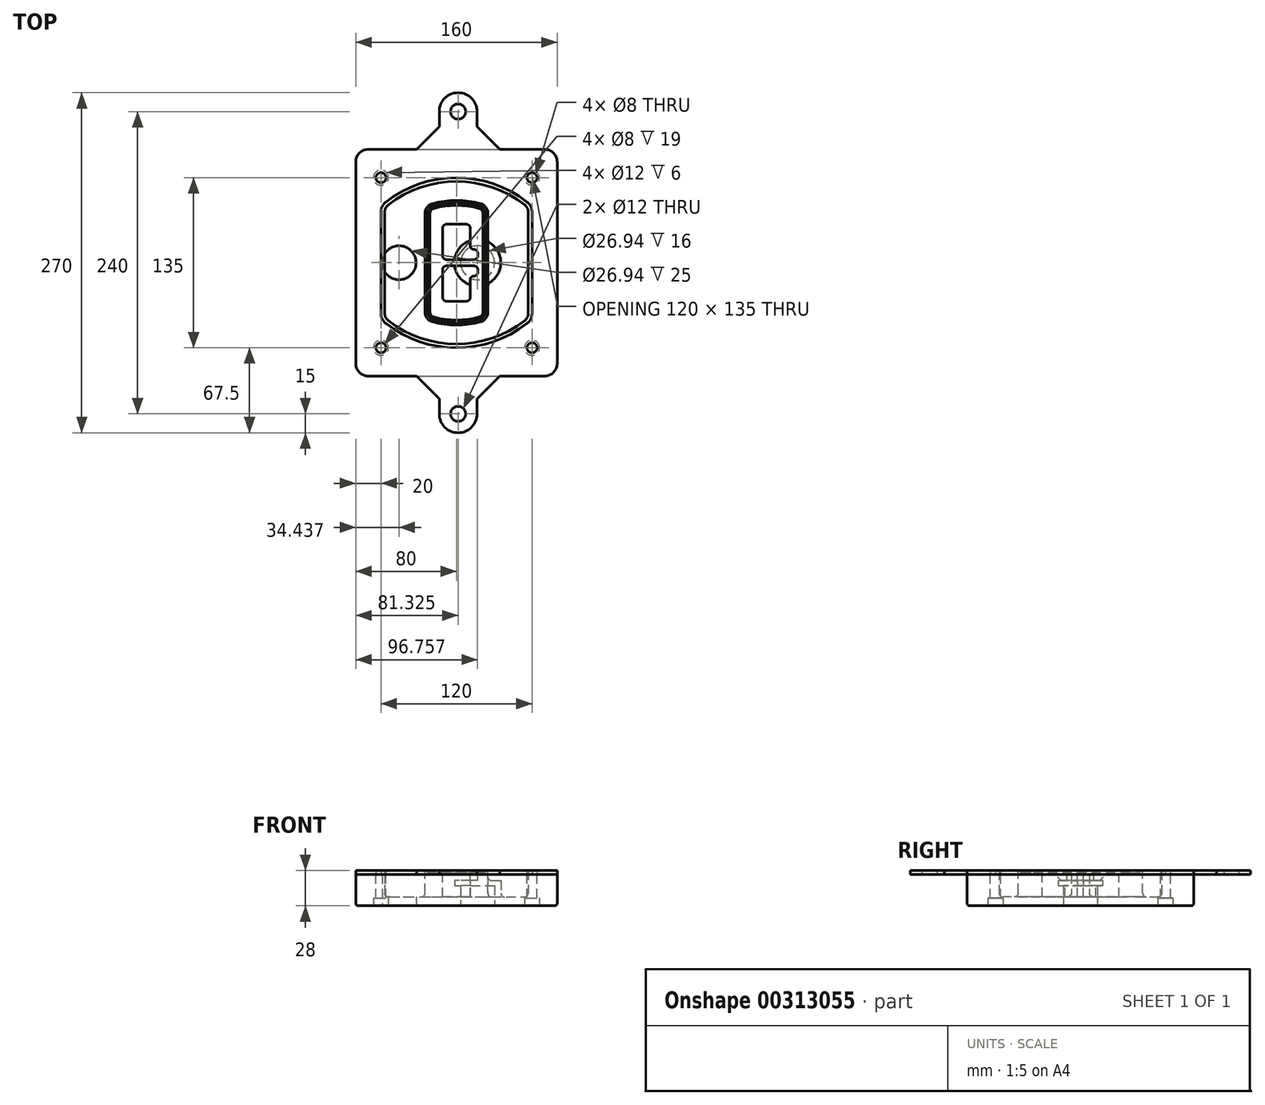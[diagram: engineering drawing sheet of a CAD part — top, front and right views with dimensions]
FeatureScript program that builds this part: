
annotation { "Feature Type Name" : "Feature", "Feature Type Description" : "" }
export const myFeature = defineFeature(function(context is Context, id is Id, definition is map)
    precondition{}
    {
        {
            var Q0;
            Q0=qCreatedBy(makeId("Top.planeOp"),FACE);
            var sketch = newSketch(context, id + "F0", { "sketchPlane" : qUnion([Q0])});
            skPoint(sketch, "E0.rect.middle", {"position": v(0, 0) * mm});
            skLineSegment(sketch, "E1.bottom", {"start": v(-70, -90) * mm, "end": v(70, -90) * mm});
            skLineSegment(sketch, "E1.top", {"start": v(-70, 90) * mm, "end": v(70, 90) * mm});
            skLineSegment(sketch, "E1.left", {"start": v(-80, -80) * mm, "end": v(-80, 80) * mm});
            skLineSegment(sketch, "E1.right", {"start": v(80, -80) * mm, "end": v(80, 80) * mm});
            skLineSegment(sketch, "E2", {"start": v(-80, 90) * mm, "end": v(80, -90) * mm, "construction": true});
            skLineSegment(sketch, "E3", {"start": v(80, 90) * mm, "end": v(-80, -90) * mm, "construction": true});
            skCircle(sketch, "E4", {"center": v(-60, 67.5) * mm, "radius": 4 * mm});
            skCircle(sketch, "E5", {"center": v(60, 67.5) * mm, "radius": 4 * mm});
            skCircle(sketch, "E6", {"center": v(60, -67.5) * mm, "radius": 4 * mm});
            skCircle(sketch, "E7", {"center": v(-60, -67.5) * mm, "radius": 4 * mm});
            skLineSegment(sketch, "E8", {"start": v(-60, 67.5) * mm, "end": v(60, 67.5) * mm, "construction": true});
            skLineSegment(sketch, "E9", {"start": v(60, 67.5) * mm, "end": v(60, -67.5) * mm, "construction": true});
            skLineSegment(sketch, "E10", {"start": v(60, -67.5) * mm, "end": v(-60, -67.5) * mm, "construction": true});
            skLineSegment(sketch, "E11", {"start": v(-60, -67.5) * mm, "end": v(-60, 67.5) * mm, "construction": true});
            skLineSegment(sketch, "E12", {"start": v(-60, 40.3) * mm, "end": v(-60, -40.3) * mm});
            skLineSegment(sketch, "E13", {"start": v(60, 40.3) * mm, "end": v(60, -40.3) * mm});
            skArc(sketch, "E14", {"start": v(56.15, 48.18) * mm, "mid": v(0, 67.5) * mm, "end": v(-56.15, 48.18) * mm});
            skArc(sketch, "E15", {"start": v(-56.15, -48.18) * mm, "mid": v(0, -67.5) * mm, "end": v(56.15, -48.18) * mm});
            skLineSegment(sketch, "E16", {"start": v(-60, 0) * mm, "end": v(60, 0) * mm, "construction": true});
            skPoint(sketch, "E17.visualSharp", {"position": v(-60, -45) * mm});
            skArc(sketch, "E17.filletArc", {"start": v(-60, -40.3) * mm, "mid": v(-58.99, -44.68) * mm, "end": v(-56.15, -48.18) * mm});
            skPoint(sketch, "E18.visualSharp", {"position": v(-60, 45) * mm});
            skArc(sketch, "E18.filletArc", {"start": v(-56.15, 48.18) * mm, "mid": v(-58.99, 44.68) * mm, "end": v(-60, 40.3) * mm});
            skPoint(sketch, "E19.visualSharp", {"position": v(60, 45) * mm});
            skArc(sketch, "E19.filletArc", {"start": v(60, 40.3) * mm, "mid": v(58.99, 44.68) * mm, "end": v(56.15, 48.18) * mm});
            skPoint(sketch, "E20.visualSharp", {"position": v(60, -45) * mm});
            skArc(sketch, "E20.filletArc", {"start": v(56.15, -48.18) * mm, "mid": v(58.99, -44.68) * mm, "end": v(60, -40.3) * mm});
            skPoint(sketch, "E21.visualSharp", {"position": v(-80, 90) * mm});
            skArc(sketch, "E21.filletArc", {"start": v(-70, 90) * mm, "mid": v(-77.07, 87.07) * mm, "end": v(-80, 80) * mm});
            skPoint(sketch, "E22.visualSharp", {"position": v(80, 90) * mm});
            skArc(sketch, "E22.filletArc", {"start": v(80, 80) * mm, "mid": v(77.07, 87.07) * mm, "end": v(70, 90) * mm});
            skPoint(sketch, "E23.visualSharp", {"position": v(80, -90) * mm});
            skArc(sketch, "E23.filletArc", {"start": v(70, -90) * mm, "mid": v(77.07, -87.07) * mm, "end": v(80, -80) * mm});
            skPoint(sketch, "E24.visualSharp", {"position": v(-80, -90) * mm});
            skArc(sketch, "E24.filletArc", {"start": v(-80, -80) * mm, "mid": v(-77.07, -87.07) * mm, "end": v(-70, -90) * mm});
            skArc(sketch, "E25.0", {"start": v(57, 40.3) * mm, "mid": v(56.3, 43.36) * mm, "end": v(54.3, 45.81) * mm});
            skLineSegment(sketch, "E25.1", {"start": v(57, 40.3) * mm, "end": v(57, -40.3) * mm});
            skArc(sketch, "E25.2", {"start": v(54.3, -45.81) * mm, "mid": v(56.3, -43.36) * mm, "end": v(57, -40.3) * mm});
            skArc(sketch, "E25.3", {"start": v(-54.3, -45.81) * mm, "mid": v(0, -64.5) * mm, "end": v(54.3, -45.81) * mm});
            skArc(sketch, "E25.4", {"start": v(-57, -40.3) * mm, "mid": v(-56.3, -43.36) * mm, "end": v(-54.3, -45.81) * mm});
            skArc(sketch, "E25.5", {"start": v(54.3, 45.81) * mm, "mid": v(0, 64.5) * mm, "end": v(-54.3, 45.81) * mm});
            skLineSegment(sketch, "E25.6", {"start": v(-57, 40.3) * mm, "end": v(-57, -40.3) * mm});
            skArc(sketch, "E25.7", {"start": v(-54.3, 45.81) * mm, "mid": v(-56.3, 43.36) * mm, "end": v(-57, 40.3) * mm});
            skArc(sketch, "E26.0", {"start": v(-58.62, 51.33) * mm, "mid": v(-62.58, 46.43) * mm, "end": v(-64, 40.3) * mm});
            skArc(sketch, "E26.1", {"start": v(58.62, 51.33) * mm, "mid": v(0, 71.5) * mm, "end": v(-58.62, 51.33) * mm});
            skArc(sketch, "E26.2", {"start": v(64, 40.3) * mm, "mid": v(62.58, 46.43) * mm, "end": v(58.62, 51.33) * mm});
            skLineSegment(sketch, "E26.3", {"start": v(64, 40.3) * mm, "end": v(64, -40.3) * mm});
            skArc(sketch, "E26.4", {"start": v(58.62, -51.33) * mm, "mid": v(62.58, -46.43) * mm, "end": v(64, -40.3) * mm});
            skLineSegment(sketch, "E26.5", {"start": v(-64, 40.3) * mm, "end": v(-64, -40.3) * mm});
            skArc(sketch, "E26.6", {"start": v(-58.62, -51.33) * mm, "mid": v(0, -71.5) * mm, "end": v(58.62, -51.33) * mm});
            skArc(sketch, "E26.7", {"start": v(-64, -40.3) * mm, "mid": v(-62.58, -46.43) * mm, "end": v(-58.62, -51.33) * mm});
            skSolve(sketch);
        }
        {
            var Q0;
            Q0=makeQuery(id+"F0.imprint","IMPRINT",FACE,{"disambiguationData":[TD([[makeQuery(id+"F0.imprint","IMPRINT",EDGE,{"derivedFrom":sQuery(id+"F0.wireOp",EDGE,"E1.bottom")}),1.0]])]});
            var Q1;
            Q1=makeQuery(id+"F0.imprint","IMPRINT",FACE,{"disambiguationData":[TD([[makeQuery(id+"F0.imprint","IMPRINT",EDGE,{"derivedFrom":sQuery(id+"F0.wireOp",EDGE,"E12")}),1.0]])]});
            var Q2;
            Q2=makeQuery(id+"F0.imprint","IMPRINT",FACE,{"disambiguationData":[TD([[makeQuery(id+"F0.imprint","IMPRINT",EDGE,{"derivedFrom":sQuery(id+"F0.wireOp",EDGE,"E25.0")}),1.0]])]});
            var Q3;
            Q3=makeQuery(id+"F0.imprint","IMPRINT",FACE,{"disambiguationData":[TD([[makeQuery(id+"F0.imprint","IMPRINT",EDGE,{"derivedFrom":sQuery(id+"F0.wireOp",EDGE,"E12")}),-1.0]])]});
            extrude(context, id + "F1", {"entities" : qUnion([Q0, Q1, Q2, Q3]), "oppositeDirection" : true, "depth" : 25 * mm});
        }
        {
            var Q0;
            Q0=makeQuery(id+"F0.imprint","IMPRINT",FACE,{"disambiguationData":[TD([[makeQuery(id+"F0.imprint","IMPRINT",EDGE,{"derivedFrom":sQuery(id+"F0.wireOp",EDGE,"E12")}),1.0]])]});
            extrude(context, id + "F2", {"entities" : qUnion([Q0]), "operationType" : NewBodyOperationType.ADD, "depth" : 3 * mm});
        }
        {
            var Q0;
            Q0=makeQuery(id+"F0.imprint","IMPRINT",FACE,{"disambiguationData":[TD([[makeQuery(id+"F0.imprint","IMPRINT",EDGE,{"derivedFrom":sQuery(id+"F0.wireOp",EDGE,"E25.0")}),1.0]])]});
            extrude(context, id + "F3", {"entities" : qUnion([Q0]), "operationType" : NewBodyOperationType.REMOVE, "oppositeDirection" : true, "depth" : 18 * mm});
        }
        {
            var Q0;
            Q0=makeQuery(id+"F2.opExtrude","CAP_FACE",FACE,{"disambiguationData":[OSD([sQuery(id+"F0.wireOp",EDGE,"E12"),sQuery(id+"F0.wireOp",EDGE,"E13"),sQuery(id+"F0.wireOp",EDGE,"E14"),sQuery(id+"F0.wireOp",EDGE,"E15"),sQuery(id+"F0.wireOp",EDGE,"E17.filletArc"),sQuery(id+"F0.wireOp",EDGE,"E18.filletArc"),sQuery(id+"F0.wireOp",EDGE,"E19.filletArc"),sQuery(id+"F0.wireOp",EDGE,"E20.filletArc"),sQuery(id+"F0.wireOp",EDGE,"E25.0"),sQuery(id+"F0.wireOp",EDGE,"E25.1"),sQuery(id+"F0.wireOp",EDGE,"E25.2"),sQuery(id+"F0.wireOp",EDGE,"E25.3"),sQuery(id+"F0.wireOp",EDGE,"E25.4"),sQuery(id+"F0.wireOp",EDGE,"E25.5"),sQuery(id+"F0.wireOp",EDGE,"E25.6"),sQuery(id+"F0.wireOp",EDGE,"E25.7")])],"isStart":false});
            var sketch = newSketch(context, id + "F4", { "sketchPlane" : qUnion([Q0])});
            skArc(sketch, "E27.0", {"start": v(-19.08, -46.97) * mm, "mid": v(0, -49.5) * mm, "end": v(19.08, -46.97) * mm});
            skArc(sketch, "E28.0", {"start": v(19.08, 46.97) * mm, "mid": v(0, 49.5) * mm, "end": v(-19.08, 46.97) * mm});
            skLineSegment(sketch, "E29", {"start": v(-25, 39.25) * mm, "end": v(-25, -39.25) * mm});
            skLineSegment(sketch, "E30", {"start": v(25, 39.25) * mm, "end": v(25, -39.25) * mm});
            skLineSegment(sketch, "E31", {"start": v(-25, 45.1) * mm, "end": v(25, 45.1) * mm, "construction": true});
            skLineSegment(sketch, "E32", {"start": v(-25, -45.1) * mm, "end": v(25, -45.1) * mm, "construction": true});
            skPoint(sketch, "E33.visualSharp", {"position": v(-25, 45.1) * mm});
            skArc(sketch, "E33.filletArc", {"start": v(-19.08, 46.97) * mm, "mid": v(-23.35, 44.11) * mm, "end": v(-25, 39.25) * mm});
            skPoint(sketch, "E34.visualSharp", {"position": v(25, 45.1) * mm});
            skArc(sketch, "E34.filletArc", {"start": v(25, 39.25) * mm, "mid": v(23.35, 44.11) * mm, "end": v(19.08, 46.97) * mm});
            skPoint(sketch, "E35.visualSharp", {"position": v(25, -45.1) * mm});
            skArc(sketch, "E35.filletArc", {"start": v(19.08, -46.97) * mm, "mid": v(23.35, -44.11) * mm, "end": v(25, -39.25) * mm});
            skPoint(sketch, "E36.visualSharp", {"position": v(-25, -45.1) * mm});
            skArc(sketch, "E36.filletArc", {"start": v(-25, -39.25) * mm, "mid": v(-23.35, -44.11) * mm, "end": v(-19.08, -46.97) * mm});
            skArc(sketch, "E37.0", {"start": v(54.3, 45.81) * mm, "mid": v(0, 64.5) * mm, "end": v(-54.3, 45.81) * mm});
            skArc(sketch, "E37.1", {"start": v(-54.3, 45.81) * mm, "mid": v(-56.3, 43.36) * mm, "end": v(-57, 40.3) * mm});
            skLineSegment(sketch, "E37.2", {"start": v(-57, 40.3) * mm, "end": v(-57, -40.3) * mm});
            skArc(sketch, "E37.3", {"start": v(-57, -40.3) * mm, "mid": v(-56.3, -43.36) * mm, "end": v(-54.3, -45.81) * mm});
            skArc(sketch, "E37.4", {"start": v(-54.3, -45.81) * mm, "mid": v(0, -64.5) * mm, "end": v(54.3, -45.81) * mm});
            skArc(sketch, "E37.5", {"start": v(54.3, -45.81) * mm, "mid": v(56.3, -43.36) * mm, "end": v(57, -40.3) * mm});
            skLineSegment(sketch, "E37.6", {"start": v(57, 40.3) * mm, "end": v(57, -40.3) * mm});
            skArc(sketch, "E37.7", {"start": v(57, 40.3) * mm, "mid": v(56.3, 43.36) * mm, "end": v(54.3, 45.81) * mm});
            skLineSegment(sketch, "E38.0", {"start": v(23, 39.25) * mm, "end": v(23, -39.25) * mm});
            skArc(sketch, "E38.1", {"start": v(18.56, -45.04) * mm, "mid": v(21.76, -42.9) * mm, "end": v(23, -39.25) * mm});
            skArc(sketch, "E38.2", {"start": v(-18.56, -45.04) * mm, "mid": v(0, -47.5) * mm, "end": v(18.56, -45.04) * mm});
            skArc(sketch, "E38.3", {"start": v(-23, -39.25) * mm, "mid": v(-21.76, -42.9) * mm, "end": v(-18.56, -45.04) * mm});
            skLineSegment(sketch, "E38.4", {"start": v(-23, 39.25) * mm, "end": v(-23, -39.25) * mm});
            skArc(sketch, "E38.5", {"start": v(23, 39.25) * mm, "mid": v(21.76, 42.9) * mm, "end": v(18.56, 45.04) * mm});
            skArc(sketch, "E38.6", {"start": v(-18.56, 45.04) * mm, "mid": v(-21.76, 42.9) * mm, "end": v(-23, 39.25) * mm});
            skArc(sketch, "E38.7", {"start": v(18.56, 45.04) * mm, "mid": v(0, 47.5) * mm, "end": v(-18.56, 45.04) * mm});
            skArc(sketch, "E39.0", {"start": v(21, 39.25) * mm, "mid": v(20.18, 41.68) * mm, "end": v(18.04, 43.1) * mm});
            skLineSegment(sketch, "E39.1", {"start": v(21, 39.25) * mm, "end": v(21, -39.25) * mm});
            skArc(sketch, "E39.2", {"start": v(18.04, -43.1) * mm, "mid": v(20.18, -41.68) * mm, "end": v(21, -39.25) * mm});
            skArc(sketch, "E39.3", {"start": v(-18.04, -43.1) * mm, "mid": v(0, -45.5) * mm, "end": v(18.04, -43.1) * mm});
            skArc(sketch, "E39.4", {"start": v(-21, -39.25) * mm, "mid": v(-20.18, -41.68) * mm, "end": v(-18.04, -43.1) * mm});
            skArc(sketch, "E39.5", {"start": v(18.04, 43.1) * mm, "mid": v(0, 45.5) * mm, "end": v(-18.04, 43.1) * mm});
            skLineSegment(sketch, "E39.6", {"start": v(-21, 39.25) * mm, "end": v(-21, -39.25) * mm});
            skArc(sketch, "E39.7", {"start": v(-18.04, 43.1) * mm, "mid": v(-20.18, 41.68) * mm, "end": v(-21, 39.25) * mm});
            skLineSegment(sketch, "E40", {"start": v(-25, 0) * mm, "end": v(25, 0) * mm, "construction": true});
            skLineSegment(sketch, "E41", {"start": v(-11, 5.5) * mm, "end": v(-11, 27.5) * mm});
            skLineSegment(sketch, "E42", {"start": v(-8, 30.5) * mm, "end": v(8, 30.5) * mm});
            skLineSegment(sketch, "E43", {"start": v(11, 27.5) * mm, "end": v(11, 13.5) * mm});
            skLineSegment(sketch, "E44", {"start": v(14, 10.5) * mm, "end": v(14, 10.5) * mm});
            skLineSegment(sketch, "E45", {"start": v(17, 7.5) * mm, "end": v(17, 5.5) * mm});
            skLineSegment(sketch, "E46", {"start": v(14, 2.5) * mm, "end": v(-8, 2.5) * mm});
            skPoint(sketch, "E47.visualSharp", {"position": v(-11, 30.5) * mm});
            skArc(sketch, "E47.filletArc", {"start": v(-8, 30.5) * mm, "mid": v(-10.12, 29.62) * mm, "end": v(-11, 27.5) * mm});
            skPoint(sketch, "E48.visualSharp", {"position": v(11, 30.5) * mm});
            skArc(sketch, "E48.filletArc", {"start": v(11, 27.5) * mm, "mid": v(10.12, 29.62) * mm, "end": v(8, 30.5) * mm});
            skPoint(sketch, "E49.visualSharp", {"position": v(11, 10.5) * mm});
            skArc(sketch, "E49.filletArc", {"start": v(11, 13.5) * mm, "mid": v(11.88, 11.38) * mm, "end": v(14, 10.5) * mm});
            skPoint(sketch, "E50.visualSharp", {"position": v(17, 10.5) * mm});
            skArc(sketch, "E50.filletArc", {"start": v(17, 7.5) * mm, "mid": v(16.12, 9.62) * mm, "end": v(14, 10.5) * mm});
            skPoint(sketch, "E51.visualSharp", {"position": v(17, 2.5) * mm});
            skArc(sketch, "E51.filletArc", {"start": v(14, 2.5) * mm, "mid": v(16.12, 3.38) * mm, "end": v(17, 5.5) * mm});
            skPoint(sketch, "E52.visualSharp", {"position": v(-11, 2.5) * mm});
            skArc(sketch, "E52.filletArc", {"start": v(-11, 5.5) * mm, "mid": v(-10.12, 3.38) * mm, "end": v(-8, 2.5) * mm});
            skLineSegment(sketch, "E53.0.MirrorCS", {"start": v(14, -2.5) * mm, "end": v(-8, -2.5) * mm});
            skArc(sketch, "E54.0.MirrorCS", {"start": v(-11, -5.5) * mm, "mid": v(-10.12, -3.38) * mm, "end": v(-8, -2.5) * mm});
            skLineSegment(sketch, "E55.0.MirrorCS", {"start": v(-11, -5.5) * mm, "end": v(-11, -27.5) * mm});
            skArc(sketch, "E56.0.MirrorCS", {"start": v(-8, -30.5) * mm, "mid": v(-10.12, -29.62) * mm, "end": v(-11, -27.5) * mm});
            skLineSegment(sketch, "E57.0.MirrorCS", {"start": v(-8, -30.5) * mm, "end": v(8, -30.5) * mm});
            skArc(sketch, "E58.0.MirrorCS", {"start": v(11, -27.5) * mm, "mid": v(10.12, -29.62) * mm, "end": v(8, -30.5) * mm});
            skLineSegment(sketch, "E59.0.MirrorCS", {"start": v(11, -27.5) * mm, "end": v(11, -13.5) * mm});
            skArc(sketch, "E60.0.MirrorCS", {"start": v(11, -13.5) * mm, "mid": v(11.88, -11.38) * mm, "end": v(14, -10.5) * mm});
            skArc(sketch, "E61.0.MirrorCS", {"start": v(17, -7.5) * mm, "mid": v(16.12, -9.62) * mm, "end": v(14, -10.5) * mm});
            skLineSegment(sketch, "E62.0.MirrorCS", {"start": v(17, -7.5) * mm, "end": v(17, -5.5) * mm});
            skArc(sketch, "E63.0.MirrorCS", {"start": v(14, -2.5) * mm, "mid": v(16.12, -3.38) * mm, "end": v(17, -5.5) * mm});
            skSolve(sketch);
        }
        {
            var Q0;
            Q0=makeQuery(id+"F4.imprint","IMPRINT",FACE,{"disambiguationData":[TD([[makeQuery(id+"F4.imprint","IMPRINT",EDGE,{"derivedFrom":sQuery(id+"F4.wireOp",EDGE,"E27.0")}),1.0]])]});
            var Q1;
            Q1=makeQuery(id+"F4.imprint","IMPRINT",FACE,{"disambiguationData":[TD([[makeQuery(id+"F4.imprint","IMPRINT",EDGE,{"derivedFrom":sQuery(id+"F4.wireOp",EDGE,"E38.0")}),-1.0]])]});
            var Q2;
            Q2=makeQuery(id+"F4.imprint","IMPRINT",FACE,{"disambiguationData":[TD([[makeQuery(id+"F4.imprint","IMPRINT",EDGE,{"derivedFrom":sQuery(id+"F4.wireOp",EDGE,"E39.0")}),1.0]])]});
            extrude(context, id + "F5", {"entities" : qUnion([Q0, Q1, Q2]), "operationType" : NewBodyOperationType.ADD, "endBound" : BoundingType.UP_TO_NEXT, "oppositeDirection" : true, "depth" : 25 * mm});
        }
        {
            var Q0;
            Q0=makeQuery(id+"F4.imprint","IMPRINT",FACE,{"disambiguationData":[TD([[makeQuery(id+"F4.imprint","IMPRINT",EDGE,{"derivedFrom":sQuery(id+"F4.wireOp",EDGE,"E38.0")}),-1.0]])]});
            extrude(context, id + "F6", {"entities" : qUnion([Q0]), "operationType" : NewBodyOperationType.REMOVE, "oppositeDirection" : true, "depth" : 2 * mm});
        }
        {
            var Q0;
            Q0=makeQuery(id+"F1.opExtrude","CAP_FACE",FACE,{"disambiguationData":[OSD([sQuery(id+"F0.wireOp",EDGE,"E1.bottom"),sQuery(id+"F0.wireOp",EDGE,"E1.top"),sQuery(id+"F0.wireOp",EDGE,"E1.left"),sQuery(id+"F0.wireOp",EDGE,"E1.right"),sQuery(id+"F0.wireOp",EDGE,"E4"),sQuery(id+"F0.wireOp",EDGE,"E5"),sQuery(id+"F0.wireOp",EDGE,"E6"),sQuery(id+"F0.wireOp",EDGE,"E7"),sQuery(id+"F0.wireOp",EDGE,"E21.filletArc"),sQuery(id+"F0.wireOp",EDGE,"E22.filletArc"),sQuery(id+"F0.wireOp",EDGE,"E23.filletArc"),sQuery(id+"F0.wireOp",EDGE,"E24.filletArc")])],"isStart":false});
            var sketch = newSketch(context, id + "F7", { "sketchPlane" : qUnion([Q0])});
            skCircle(sketch, "E64", {"center": v(16.76, 0) * mm, "radius": 13.47 * mm});
            skCircle(sketch, "E65", {"center": v(-45.56, 0) * mm, "radius": 13.47 * mm});
            skLineSegment(sketch, "E66", {"start": v(80, 0) * mm, "end": v(-80, 0) * mm});
            skCircle(sketch, "E67", {"center": v(16.76, 0) * mm, "radius": 18.47 * mm});
            skCircle(sketch, "E68", {"center": v(60, -67.5) * mm, "radius": 6 * mm});
            skCircle(sketch, "E69", {"center": v(-60, -67.5) * mm, "radius": 6 * mm});
            skCircle(sketch, "E70", {"center": v(-60, 67.5) * mm, "radius": 6 * mm});
            skCircle(sketch, "E71", {"center": v(60, 67.5) * mm, "radius": 6 * mm});
            skSolve(sketch);
        }
        {
            var Q0;
            {var subQ1=sQuery(id+"F7.wireOp",EDGE,"E66");var subQ4=sQuery(id+"F7.wireOp",EDGE,"E64");var subQ6=makeQuery(id+"F7.imprint","INTERSECT",VERTEX,{"disambiguationData":[OD(0.0)],"derivedFrom":[subQ4,subQ1]});Q0=makeQuery(id+"F7.imprint","IMPRINT",FACE,{"disambiguationData":[TD([[makeQuery(id+"F7.imprint","IMPRINT",EDGE,{"disambiguationData":[TD([[subQ6,-1.0]])],"derivedFrom":subQ4}),-1.0]])]});}
            var Q1;
            {var subQ0=sQuery(id+"F7.wireOp",EDGE,"E66");var subQ1=sQuery(id+"F7.wireOp",EDGE,"E64");var subQ3=makeQuery(id+"F7.imprint","INTERSECT",VERTEX,{"disambiguationData":[OD(0.0)],"derivedFrom":[subQ1,subQ0]});Q1=makeQuery(id+"F7.imprint","IMPRINT",FACE,{"disambiguationData":[TD([[makeQuery(id+"F7.imprint","IMPRINT",EDGE,{"disambiguationData":[TD([[subQ3,-1.0]])],"derivedFrom":subQ1}),1.0]])]});}
            var Q2;
            {var subQ0=sQuery(id+"F7.wireOp",EDGE,"E66");var subQ1=sQuery(id+"F7.wireOp",EDGE,"E64");var subQ3=makeQuery(id+"F7.imprint","INTERSECT",VERTEX,{"disambiguationData":[OD(0.0)],"derivedFrom":[subQ1,subQ0]});Q2=makeQuery(id+"F7.imprint","IMPRINT",FACE,{"disambiguationData":[TD([[makeQuery(id+"F7.imprint","IMPRINT",EDGE,{"disambiguationData":[TD([[subQ3,1.0]])],"derivedFrom":subQ1}),1.0]])]});}
            var Q3;
            {var subQ1=sQuery(id+"F7.wireOp",EDGE,"E66");var subQ4=sQuery(id+"F7.wireOp",EDGE,"E64");var subQ6=makeQuery(id+"F7.imprint","INTERSECT",VERTEX,{"disambiguationData":[OD(0.0)],"derivedFrom":[subQ4,subQ1]});Q3=makeQuery(id+"F7.imprint","IMPRINT",FACE,{"disambiguationData":[TD([[makeQuery(id+"F7.imprint","IMPRINT",EDGE,{"disambiguationData":[TD([[subQ6,1.0]])],"derivedFrom":subQ4}),-1.0]])]});}
            extrude(context, id + "F8", {"entities" : qUnion([Q0, Q1, Q2, Q3]), "operationType" : NewBodyOperationType.ADD, "oppositeDirection" : true, "depth" : 20 * mm});
        }
        {
            var Q0;
            {var subQ0=sQuery(id+"F7.wireOp",EDGE,"E66");var subQ1=sQuery(id+"F7.wireOp",EDGE,"E64");var subQ3=makeQuery(id+"F7.imprint","INTERSECT",VERTEX,{"disambiguationData":[OD(0.0)],"derivedFrom":[subQ1,subQ0]});Q0=makeQuery(id+"F7.imprint","IMPRINT",FACE,{"disambiguationData":[TD([[makeQuery(id+"F7.imprint","IMPRINT",EDGE,{"disambiguationData":[TD([[subQ3,-1.0]])],"derivedFrom":subQ1}),1.0]])]});}
            var Q1;
            {var subQ0=sQuery(id+"F7.wireOp",EDGE,"E66");var subQ1=sQuery(id+"F7.wireOp",EDGE,"E64");var subQ3=makeQuery(id+"F7.imprint","INTERSECT",VERTEX,{"disambiguationData":[OD(0.0)],"derivedFrom":[subQ1,subQ0]});Q1=makeQuery(id+"F7.imprint","IMPRINT",FACE,{"disambiguationData":[TD([[makeQuery(id+"F7.imprint","IMPRINT",EDGE,{"disambiguationData":[TD([[subQ3,1.0]])],"derivedFrom":subQ1}),1.0]])]});}
            extrude(context, id + "F9", {"entities" : qUnion([Q0, Q1]), "operationType" : NewBodyOperationType.REMOVE, "oppositeDirection" : true, "depth" : 16 * mm});
        }
        {
            var Q0;
            {var subQ0=sQuery(id+"F7.wireOp",EDGE,"E66");var subQ1=sQuery(id+"F7.wireOp",EDGE,"E65");var subQ3=makeQuery(id+"F7.imprint","INTERSECT",VERTEX,{"disambiguationData":[OD(0.0)],"derivedFrom":[subQ1,subQ0]});Q0=makeQuery(id+"F7.imprint","IMPRINT",FACE,{"disambiguationData":[TD([[makeQuery(id+"F7.imprint","IMPRINT",EDGE,{"disambiguationData":[TD([[subQ3,-1.0]])],"derivedFrom":subQ1}),1.0]])]});}
            var Q1;
            {var subQ0=sQuery(id+"F7.wireOp",EDGE,"E66");var subQ1=sQuery(id+"F7.wireOp",EDGE,"E65");var subQ3=makeQuery(id+"F7.imprint","INTERSECT",VERTEX,{"disambiguationData":[OD(0.0)],"derivedFrom":[subQ1,subQ0]});Q1=makeQuery(id+"F7.imprint","IMPRINT",FACE,{"disambiguationData":[TD([[makeQuery(id+"F7.imprint","IMPRINT",EDGE,{"disambiguationData":[TD([[subQ3,1.0]])],"derivedFrom":subQ1}),1.0]])]});}
            extrude(context, id + "F10", {"entities" : qUnion([Q0, Q1]), "operationType" : NewBodyOperationType.REMOVE, "oppositeDirection" : true, "depth" : 25 * mm});
        }
        {
            var Q0;
            Q0=makeQuery(id+"F7.imprint","IMPRINT",FACE,{"disambiguationData":[TD([[makeQuery(id+"F7.imprint","IMPRINT",EDGE,{"derivedFrom":sQuery(id+"F7.wireOp",EDGE,"E68")}),1.0]])]});
            var Q1;
            Q1=makeQuery(id+"F7.imprint","IMPRINT",FACE,{"disambiguationData":[TD([[makeQuery(id+"F7.imprint","IMPRINT",EDGE,{"derivedFrom":makeQuery(id+"F1.opExtrude","CAP_EDGE",EDGE,{"disambiguationData":[OSD([sQuery(id+"F0.wireOp",EDGE,"E5")])],"isStart":false})}),-1.0]])]});
            var Q2;
            Q2=makeQuery(id+"F7.imprint","IMPRINT",FACE,{"disambiguationData":[TD([[makeQuery(id+"F7.imprint","IMPRINT",EDGE,{"derivedFrom":sQuery(id+"F7.wireOp",EDGE,"E69")}),1.0]])]});
            var Q3;
            Q3=makeQuery(id+"F7.imprint","IMPRINT",FACE,{"disambiguationData":[TD([[makeQuery(id+"F7.imprint","IMPRINT",EDGE,{"derivedFrom":makeQuery(id+"F1.opExtrude","CAP_EDGE",EDGE,{"disambiguationData":[OSD([sQuery(id+"F0.wireOp",EDGE,"E4")])],"isStart":false})}),-1.0]])]});
            var Q4;
            Q4=makeQuery(id+"F7.imprint","IMPRINT",FACE,{"disambiguationData":[TD([[makeQuery(id+"F7.imprint","IMPRINT",EDGE,{"derivedFrom":sQuery(id+"F7.wireOp",EDGE,"E70")}),1.0]])]});
            var Q5;
            Q5=makeQuery(id+"F7.imprint","IMPRINT",FACE,{"disambiguationData":[TD([[makeQuery(id+"F7.imprint","IMPRINT",EDGE,{"derivedFrom":makeQuery(id+"F1.opExtrude","CAP_EDGE",EDGE,{"disambiguationData":[OSD([sQuery(id+"F0.wireOp",EDGE,"E7")])],"isStart":false})}),-1.0]])]});
            var Q6;
            Q6=makeQuery(id+"F7.imprint","IMPRINT",FACE,{"disambiguationData":[TD([[makeQuery(id+"F7.imprint","IMPRINT",EDGE,{"derivedFrom":sQuery(id+"F7.wireOp",EDGE,"E71")}),1.0]])]});
            var Q7;
            Q7=makeQuery(id+"F7.imprint","IMPRINT",FACE,{"disambiguationData":[TD([[makeQuery(id+"F7.imprint","IMPRINT",EDGE,{"derivedFrom":makeQuery(id+"F1.opExtrude","CAP_EDGE",EDGE,{"disambiguationData":[OSD([sQuery(id+"F0.wireOp",EDGE,"E6")])],"isStart":false})}),-1.0]])]});
            extrude(context, id + "F11", {"entities" : qUnion([Q0, Q1, Q2, Q3, Q4, Q5, Q6, Q7]), "operationType" : NewBodyOperationType.REMOVE, "oppositeDirection" : true, "depth" : 6 * mm});
        }
        {
            var Q0;
            Q0=makeQuery(id+"F9.boolean.opBoolean","COPY",FACE,{"derivedFrom":makeQuery(id+"F9.opExtrude","CAP_FACE",FACE,{"disambiguationData":[OSD([sQuery(id+"F7.wireOp",EDGE,"E64")])],"isStart":false})});
            var sketch = newSketch(context, id + "F12", { "sketchPlane" : qUnion([Q0])});
            skArc(sketch, "E72.0", {"start": v(11, 17.55) * mm, "mid": v(2.57, 11.82) * mm, "end": v(-1.54, 2.5) * mm});
            skArc(sketch, "E72.1", {"start": v(-1.54, -2.5) * mm, "mid": v(2.57, -11.82) * mm, "end": v(11, -17.55) * mm});
            skLineSegment(sketch, "E73", {"start": v(-1.54, -2.5) * mm, "end": v(14, -2.5) * mm});
            skLineSegment(sketch, "E74.0", {"start": v(14, 2.5) * mm, "end": v(-1.54, 2.5) * mm});
            skArc(sketch, "E74.1", {"start": v(14, 2.5) * mm, "mid": v(16.12, 3.38) * mm, "end": v(17, 5.5) * mm});
            skLineSegment(sketch, "E74.2", {"start": v(17, 7.5) * mm, "end": v(17, 5.5) * mm});
            skArc(sketch, "E74.3", {"start": v(17, 7.5) * mm, "mid": v(16.12, 9.62) * mm, "end": v(14, 10.5) * mm});
            skArc(sketch, "E74.4", {"start": v(11, 13.5) * mm, "mid": v(11.88, 11.38) * mm, "end": v(14, 10.5) * mm});
            skLineSegment(sketch, "E74.5", {"start": v(11, 17.55) * mm, "end": v(11, 13.5) * mm});
            skLineSegment(sketch, "E74.7", {"start": v(14, -2.5) * mm, "end": v(-1.54, -2.5) * mm});
            skArc(sketch, "E74.8", {"start": v(14, -2.5) * mm, "mid": v(16.12, -3.38) * mm, "end": v(17, -5.5) * mm});
            skLineSegment(sketch, "E74.9", {"start": v(17, -7.5) * mm, "end": v(17, -5.5) * mm});
            skArc(sketch, "E74.10", {"start": v(17, -7.5) * mm, "mid": v(16.12, -9.62) * mm, "end": v(14, -10.5) * mm});
            skArc(sketch, "E74.11", {"start": v(11, -13.5) * mm, "mid": v(11.88, -11.38) * mm, "end": v(14, -10.5) * mm});
            skLineSegment(sketch, "E74.12", {"start": v(11, -17.55) * mm, "end": v(11, -13.5) * mm});
            skPoint(sketch, "E75.orphan", {"position": v(11, -27.5) * mm});
            skPoint(sketch, "E76.orphan", {"position": v(-8, -2.5) * mm});
            skPoint(sketch, "E77.orphan", {"position": v(-8, 2.5) * mm});
            skPoint(sketch, "E78.orphan", {"position": v(11, 27.5) * mm});
            skSolve(sketch);
        }
        {
            var Q0;
            {var subQ7=sQuery(id+"F12.wireOp",EDGE,"E72.0");var subQ14=sQuery(id+"F12.wireOp",EDGE,"E72.1");var subQ16=sQuery(id+"F12.wireOp",EDGE,"E74.1");var subQ18=sQuery(id+"F12.wireOp",EDGE,"E74.8");Q0=qUnion([makeQuery(id+"F12.imprint","IMPRINT",FACE,{"disambiguationData":[TD([[makeQuery(id+"F12.imprint","IMPRINT",EDGE,{"derivedFrom":subQ7}),1.0]])]}),makeQuery(id+"F12.imprint","IMPRINT",FACE,{"disambiguationData":[TD([[makeQuery(id+"F12.imprint","IMPRINT",EDGE,{"derivedFrom":subQ14}),1.0]])]}),makeQuery(id+"F12.imprint","IMPRINT",FACE,{"disambiguationData":[TD([[makeQuery(id+"F12.imprint","IMPRINT",EDGE,{"derivedFrom":subQ16}),1.0]])]}),makeQuery(id+"F12.imprint","IMPRINT",FACE,{"disambiguationData":[TD([[makeQuery(id+"F12.imprint","IMPRINT",EDGE,{"derivedFrom":subQ18}),-1.0]])]})]);}
            var Q1;
            Q1=makeQuery(id+"F5.boolean.opBoolean","SPLIT",FACE,{"disambiguationData":[TD([makeQuery(id+"F5.opExtrude","SWEPT_FACE",FACE,{"disambiguationData":[OSD([sQuery(id+"F4.wireOp",EDGE,"E41")])]})])],"derivedFrom":makeQuery(id+"F3.boolean.opBoolean","COPY",FACE,{"derivedFrom":makeQuery(id+"F3.opExtrude","CAP_FACE",FACE,{"disambiguationData":[OSD([sQuery(id+"F0.wireOp",EDGE,"E25.0"),sQuery(id+"F0.wireOp",EDGE,"E25.1"),sQuery(id+"F0.wireOp",EDGE,"E25.2"),sQuery(id+"F0.wireOp",EDGE,"E25.3"),sQuery(id+"F0.wireOp",EDGE,"E25.4"),sQuery(id+"F0.wireOp",EDGE,"E25.5"),sQuery(id+"F0.wireOp",EDGE,"E25.6"),sQuery(id+"F0.wireOp",EDGE,"E25.7")])],"isStart":false})})});
            extrude(context, id + "F13", {"entities" : qUnion([Q0]), "operationType" : NewBodyOperationType.REMOVE, "endBound" : BoundingType.UP_TO_SURFACE, "endBoundEntityFace" : qUnion([Q1]), "depth" : 25 * mm});
        }
        {
            var Q0;
            Q0=makeQuery(id+"F3.boolean.opBoolean","COPY",EDGE,{"derivedFrom":makeQuery(id+"F3.opExtrude","CAP_EDGE",EDGE,{"disambiguationData":[OSD([sQuery(id+"F0.wireOp",EDGE,"E25.6")])],"isStart":false})});
            var Q1;
            Q1=makeQuery(id+"F8.boolean.opBoolean","INTERSECT",EDGE,{"derivedFrom":[makeQuery(id+"F5.opExtrude","SWEPT_FACE",FACE,{"disambiguationData":[OSD([sQuery(id+"F4.wireOp",EDGE,"E30")])]}),makeQuery(id+"F8.opExtrude","CAP_FACE",FACE,{"disambiguationData":[OSD([sQuery(id+"F7.wireOp",EDGE,"E67")])],"isStart":false})]});
            var Q2;
            Q2=makeQuery(id+"F8.boolean.opBoolean","INTERSECT",EDGE,{"disambiguationData":[OD(1.0)],"derivedFrom":[makeQuery(id+"F5.opExtrude","SWEPT_FACE",FACE,{"disambiguationData":[OSD([sQuery(id+"F4.wireOp",EDGE,"E30")])]}),makeQuery(id+"F8.opExtrude","SWEPT_FACE",FACE,{"disambiguationData":[OSD([sQuery(id+"F7.wireOp",EDGE,"E67")])]})]});
            var Q3;
            {var subQ0=sQuery(id+"F4.wireOp",EDGE,"E30");Q3=makeQuery(id+"F8.boolean.opBoolean","SPLIT",EDGE,{"disambiguationData":[TD([makeQuery(id+"F5.opExtrude","SWEPT_FACE",FACE,{"disambiguationData":[OSD([sQuery(id+"F4.wireOp",EDGE,"E35.filletArc")])]})])],"derivedFrom":makeQuery(id+"F5.opExtrude","CAP_EDGE",EDGE,{"disambiguationData":[OSD([subQ0])],"isStart":false})});}
            var Q4;
            {var subQ0=sQuery(id+"F0.wireOp",EDGE,"E25.7");var subQ1=sQuery(id+"F0.wireOp",EDGE,"E25.1");var subQ2=sQuery(id+"F0.wireOp",EDGE,"E25.6");var subQ3=sQuery(id+"F0.wireOp",EDGE,"E25.5");var subQ4=sQuery(id+"F0.wireOp",EDGE,"E25.4");var subQ5=sQuery(id+"F0.wireOp",EDGE,"E25.0");var subQ6=sQuery(id+"F0.wireOp",EDGE,"E25.2");var subQ7=sQuery(id+"F0.wireOp",EDGE,"E25.3");Q4=makeQuery(id+"F8.boolean.opBoolean","INTERSECT",EDGE,{"derivedFrom":[makeQuery(id+"F5.boolean.opBoolean","SPLIT",FACE,{"disambiguationData":[TD([makeQuery(id+"F2.opExtrude","SWEPT_FACE",FACE,{"disambiguationData":[OSD([subQ5])]})])],"derivedFrom":makeQuery(id+"F3.boolean.opBoolean","COPY",FACE,{"derivedFrom":makeQuery(id+"F3.opExtrude","CAP_FACE",FACE,{"disambiguationData":[OSD([subQ5,subQ1,subQ6,subQ7,subQ4,subQ3,subQ2,subQ0])],"isStart":false})})}),makeQuery(id+"F8.opExtrude","SWEPT_FACE",FACE,{"disambiguationData":[OSD([sQuery(id+"F7.wireOp",EDGE,"E67")])]})]});}
            var Q5;
            Q5=makeQuery(id+"F8.boolean.opBoolean","INTERSECT",EDGE,{"disambiguationData":[OD(0.0)],"derivedFrom":[makeQuery(id+"F5.opExtrude","SWEPT_FACE",FACE,{"disambiguationData":[OSD([sQuery(id+"F4.wireOp",EDGE,"E30")])]}),makeQuery(id+"F8.opExtrude","SWEPT_FACE",FACE,{"disambiguationData":[OSD([sQuery(id+"F7.wireOp",EDGE,"E67")])]})]});
            fillet(context, id + "F14", {"entities" : qUnion([Q0, Q1, Q2, Q3, Q4, Q5]), "radius" : 3 * mm, "tangentPropagation" : true, "allowEdgeOverflow" : false});
        }
        {
            var Q0;
            Q0=makeQuery(id+"F1.opExtrude","CAP_EDGE",EDGE,{"disambiguationData":[OSD([sQuery(id+"F0.wireOp",EDGE,"E1.bottom")])],"isStart":false});
            fillet(context, id + "F15", {"entities" : qUnion([Q0]), "radius" : 2 * mm, "tangentPropagation" : true, "allowEdgeOverflow" : false});
        }
        {
            var Q0;
            {var subQ0=sQuery(id+"F0.wireOp",EDGE,"E21.filletArc");var subQ1=sQuery(id+"F0.wireOp",EDGE,"E7");var subQ2=sQuery(id+"F0.wireOp",EDGE,"E6");var subQ3=sQuery(id+"F0.wireOp",EDGE,"E5");var subQ4=sQuery(id+"F0.wireOp",EDGE,"E4");var subQ5=sQuery(id+"F0.wireOp",EDGE,"E22.filletArc");var subQ6=sQuery(id+"F0.wireOp",EDGE,"E1.bottom");var subQ7=sQuery(id+"F0.wireOp",EDGE,"E1.right");var subQ8=sQuery(id+"F0.wireOp",EDGE,"E1.top");var subQ9=sQuery(id+"F0.wireOp",EDGE,"E1.left");var subQ10=sQuery(id+"F0.wireOp",EDGE,"E23.filletArc");var subQ11=sQuery(id+"F0.wireOp",EDGE,"E24.filletArc");Q0=makeQuery(id+"F2.boolean.opBoolean","SPLIT",FACE,{"disambiguationData":[TD([makeQuery(id+"F1.opExtrude","SWEPT_FACE",FACE,{"disambiguationData":[OSD([subQ6])]})])],"derivedFrom":makeQuery(id+"F1.opExtrude","CAP_FACE",FACE,{"disambiguationData":[OSD([subQ6,subQ8,subQ9,subQ7,subQ4,subQ3,subQ2,subQ1,subQ0,subQ5,subQ10,subQ11])],"isStart":true})});}
            var sketch = newSketch(context, id + "F16", { "sketchPlane" : qUnion([Q0])});
            skLineSegment(sketch, "E79", {"start": v(-13.68, 108) * mm, "end": v(-13.68, 120) * mm});
            skLineSegment(sketch, "E80", {"start": v(16.32, 108) * mm, "end": v(16.32, 120) * mm});
            skArc(sketch, "E81", {"start": v(16.32, 120) * mm, "mid": v(1.32, 135) * mm, "end": v(-13.68, 120) * mm});
            skCircle(sketch, "E82", {"center": v(1.32, 120) * mm, "radius": 6 * mm});
            skLineSegment(sketch, "E83", {"start": v(-13.68, 108) * mm, "end": v(-31.68, 90) * mm});
            skLineSegment(sketch, "E84", {"start": v(16.32, 108) * mm, "end": v(34.32, 90) * mm});
            skLineSegment(sketch, "E85", {"start": v(-76.13, 0) * mm, "end": v(74.53, 0) * mm, "construction": true});
            skLineSegment(sketch, "E86.MirrorCS", {"start": v(-13.68, -108) * mm, "end": v(-13.68, -120) * mm});
            skLineSegment(sketch, "E87.MirrorCS", {"start": v(16.32, -108) * mm, "end": v(16.32, -120) * mm});
            skLineSegment(sketch, "E88.MirrorCS", {"start": v(16.32, -108) * mm, "end": v(34.32, -90) * mm});
            skLineSegment(sketch, "E89.MirrorCS", {"start": v(-13.68, -108) * mm, "end": v(-31.68, -90) * mm});
            skCircle(sketch, "E90.MirrorC", {"center": v(1.32, -120) * mm, "radius": 6 * mm});
            skArc(sketch, "E91.MirrorCS", {"start": v(16.32, -120) * mm, "mid": v(1.32, -135) * mm, "end": v(-13.68, -120) * mm});
            skSolve(sketch);
        }
        {
            var Q0;
            Q0=makeQuery(id+"F16.imprint","IMPRINT",FACE,{"disambiguationData":[TD([[makeQuery(id+"F16.imprint","IMPRINT",EDGE,{"derivedFrom":sQuery(id+"F16.wireOp",EDGE,"E86.MirrorCS")}),1.0]])]});
            var Q1;
            Q1=makeQuery(id+"F16.imprint","IMPRINT",FACE,{"disambiguationData":[TD([[makeQuery(id+"F16.imprint","IMPRINT",EDGE,{"derivedFrom":makeQuery(id+"F1.opExtrude","CAP_EDGE",EDGE,{"disambiguationData":[OSD([sQuery(id+"F0.wireOp",EDGE,"E1.left")])],"isStart":true})}),-1.0]])]});
            var Q2;
            Q2=makeQuery(id+"F16.imprint","IMPRINT",FACE,{"disambiguationData":[TD([[makeQuery(id+"F16.imprint","IMPRINT",EDGE,{"derivedFrom":sQuery(id+"F16.wireOp",EDGE,"E79")}),-1.0]])]});
            var Q3;
            Q3=makeQuery(id+"F2.opExtrude","CAP_FACE",FACE,{"disambiguationData":[OSD([sQuery(id+"F0.wireOp",EDGE,"E12"),sQuery(id+"F0.wireOp",EDGE,"E13"),sQuery(id+"F0.wireOp",EDGE,"E14"),sQuery(id+"F0.wireOp",EDGE,"E15"),sQuery(id+"F0.wireOp",EDGE,"E17.filletArc"),sQuery(id+"F0.wireOp",EDGE,"E18.filletArc"),sQuery(id+"F0.wireOp",EDGE,"E19.filletArc"),sQuery(id+"F0.wireOp",EDGE,"E20.filletArc"),sQuery(id+"F0.wireOp",EDGE,"E25.0"),sQuery(id+"F0.wireOp",EDGE,"E25.1"),sQuery(id+"F0.wireOp",EDGE,"E25.2"),sQuery(id+"F0.wireOp",EDGE,"E25.3"),sQuery(id+"F0.wireOp",EDGE,"E25.4"),sQuery(id+"F0.wireOp",EDGE,"E25.5"),sQuery(id+"F0.wireOp",EDGE,"E25.6"),sQuery(id+"F0.wireOp",EDGE,"E25.7")])],"isStart":false});
            extrude(context, id + "F17", {"entities" : qUnion([Q0, Q1, Q2]), "endBound" : BoundingType.UP_TO_SURFACE, "endBoundEntityFace" : qUnion([Q3]), "depth" : 25 * mm});
        }
    });
